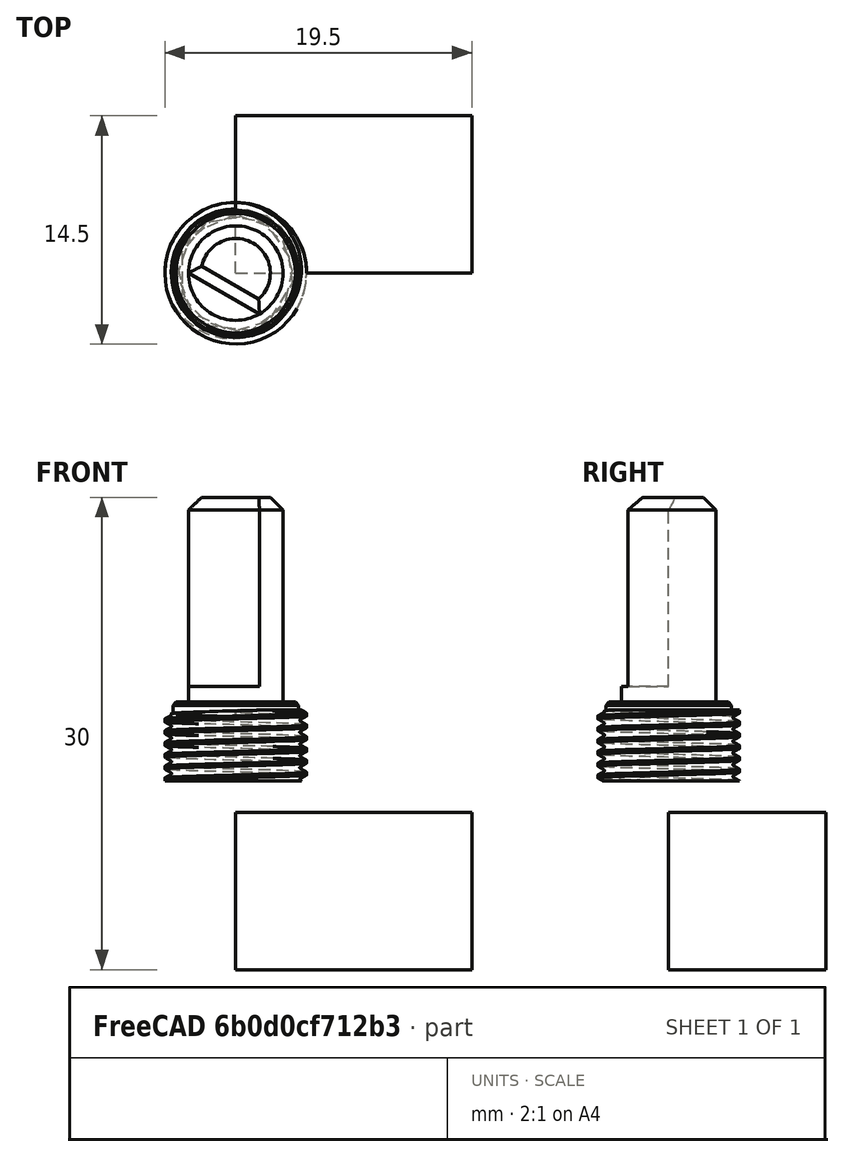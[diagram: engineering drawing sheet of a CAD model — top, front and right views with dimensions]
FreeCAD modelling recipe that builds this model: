
FCSTD DOCUMENT  (FreeCAD 0.18R16146 (Git))
Label: RV09AF-40-20K-A54
License: All rights reserved
LicenseURL: http://en.wikipedia.org/wiki/All_rights_reserved
objects: Part::Box×2, Part::Feature×1, PartDesign::Plane×1, PartDesign::Body×1, Part::Cut×1
note: 6 computed .brp shape members not serialized (recipe doc carries the construction recipe); baked Part::Feature solids carry a one-line shape summary decoded from their .brp

FEATURE [Part::Feature] Part__Feature  label="RK09L11-L200"
  Placement = pos=(0,0,7.5) rot=(1,0,0;3.14159rad)
  shape: bbox 12.1 x 12.58 x 33.5 mm, 427 faces (baked)
FEATURE [Part::Box] Box  label="Würfel"
  AttacherType = Attacher::AttachEngine3D
  Height = 17
  Length = 15
  Placement = pos=(-7,-7,-5) rot=(0,0,1;0rad)
  Width = 15
FEATURE [PartDesign::Plane] DatumPlane
  Length = 24
  MapMode = 2
  Placement = pos=(0,0,8.6) rot=(0,0,1;0rad)
  ResizeMode = 0
  Width = 24
FEATURE [PartDesign::Body] Body
  Group = -> [DatumPlane]
  Origin = -> Origin
FEATURE [Part::Cut] Cut
  Base = -> Part__Feature
  Tool = -> Box
FEATURE [Part::Box] Box001  label="RD901F-40-15R1"
  AttacherType = Attacher::AttachEngine3D
  Height = 10
  Length = 15
  Width = 10
